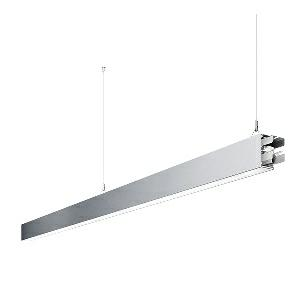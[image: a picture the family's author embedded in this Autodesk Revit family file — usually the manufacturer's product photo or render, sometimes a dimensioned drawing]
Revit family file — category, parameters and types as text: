
# Revit family: dotoo_line_-_dlp_3000_830_d_mid_00805853_dc61
name_source: partatom
category: Lighting Fixtures
units: mm (PartAtom-declared; Revit-internal decimal feet)

## family parameters
Cut with Voids When Loaded = No
Host = Face
Light Source = No
Part Type = Normal
Room Calculation Point = No
Round Connector Dimension = Use Diameter
Shared = No

## types (1)
- DOTOO.line - DLP 3000/830/D MID (1 x LED, 2650 lm, 3000K)
    Apparent Load = 26 VA
    Approval mark = CE
    CIE Flux Codes = 67 91 98 100 100
    Color Rendering = 80-89
    Color Temperature = 3000K
    Control Gear = Electronic ballast
    Default Elevation = 1800 mm
    Description = DLP 3000/830/D|Suspended luminaire|light source: LED|connected load: 220-240 V, 50/60 Hz|Power consumption: approx. 26 W|standby: approx. 0,15|luminous flux: 2650 lm|luminous efficacy: 101 lm/W|light distribution: Direct|direct ratio: approx. 100 %|colour temperature: Warm white, ca. 3000 K|color rendering index (CRI): >= 80|chromaticity tolerance:  3 SDCM|System of protection: IP 40|technology: Continuously dimmable|luminaire body|material: Sectional aluminium|colour: Silver|lamp cover: Acrylic (PMMA), Clear|mains lead: 1,0 m With free stranded wires|Fastening: Steel cable 0.3 - 0.7 m|glare control: Prism aperture|luminance(L65): <= 3000 cd/m|unified glare rating(4H 8H): <=  19|special features: DALI Load 1x, TouchDIM - dimming via standard switch, Through-wired, up to 18 m on one mains connection, Flicker-free, Suitable as emergency lighting, Mechanical and electrical connection of the individual modules without tools|
    Frequency = 50 Hz
    Height = 110 mm
    Lamp = 1 x LED
    Lamp Light Flux = 2650 lm
    Lamp count = 1
    Length = 2244 mm
    Luminous efficacy = 102 lm/W
    Manufacturer = Waldmann
    ModVariant = No
    Model = 00805853
    Mounting Place = Ceiling
    Mounting Type = Pendant
    Number of Poles = 1
    OnlyDefault = Yes
    Power Factor = 1
    Product Name = DOTOO.line - DLP 3000/830/D MID
    Product group = Suspended luminaire
    ProductGroupID = 9
    Protection Class = Protection class I
    Protection Degree = IP 40
    RLX_Detail_Level = 1
    RLX_Emergency_Light_Flux = 0 lm
    RLX_Emergency_Type = 0
    RLX_Emergency_Type_DB = No
    RlxData = <blob elided: 24205 chars, md5=3c9c68bb>
    Socket = socket
    Standby Power = 0 W
    System Light Flux = 2650 lm
    System Power = 26 W
    Type Comments = Product without accessories
    Type Image = 113317000-00692618.jpg
    URL = http://relux.com
    VarID = ---
    Voltage = 230 V
    Voltage Range = 220-240 V
    Weight = 0.00 kg
    Width = 60 mm  [stored 0.19685 ft]

note: [stored X ft] marks values corroborated as IEEE doubles in the binary element streams (Revit-internal decimal feet)

## geometry (parser evidence)
native form markers: Blend x4, Sweep x10
no freeform markers — native parametric forms only
